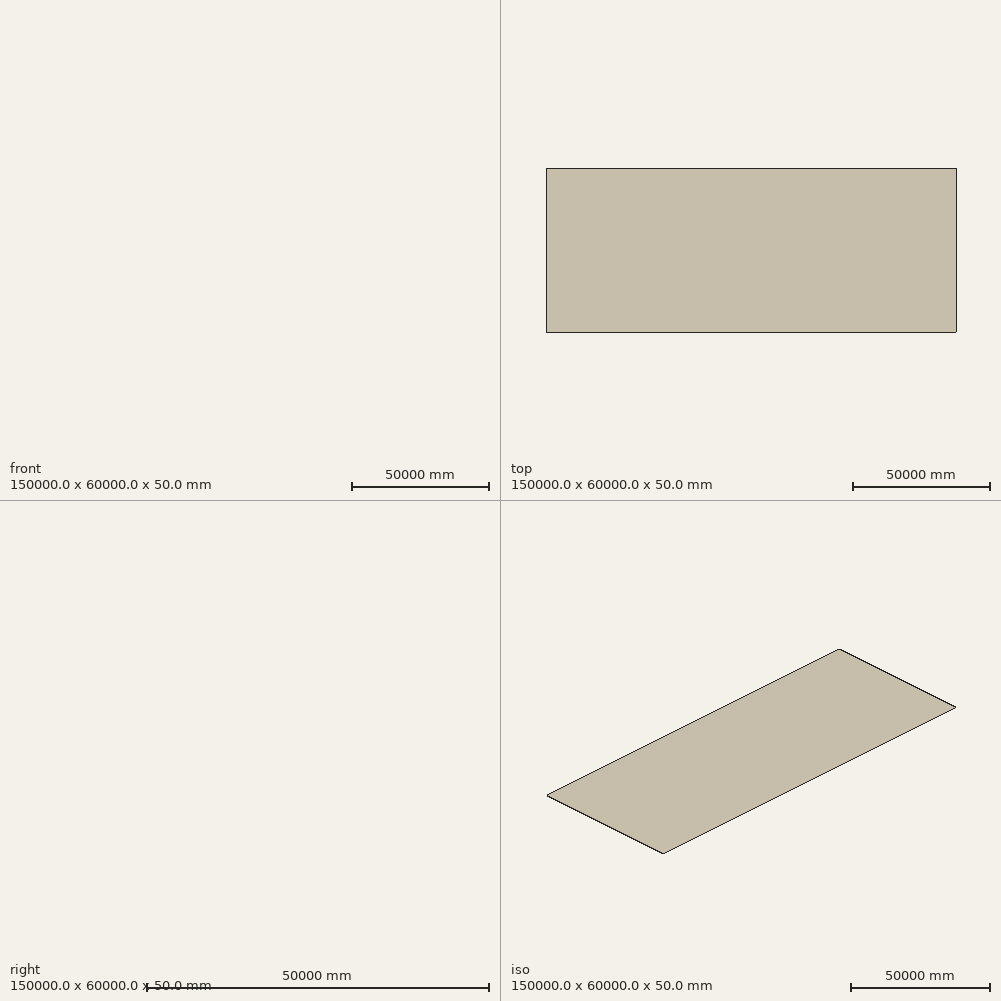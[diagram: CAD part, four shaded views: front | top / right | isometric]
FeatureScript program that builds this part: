
annotation { "Feature Type Name" : "Feature", "Feature Type Description" : "" }
export const myFeature = defineFeature(function(context is Context, id is Id, definition is map)
    precondition{}
    {
        {
            var Q0;
            Q0=qCreatedBy(makeId("Top.planeOp"),FACE);
            var sketch = newSketch(context, id + "F0", { "sketchPlane" : qUnion([Q0])});
            skLineSegment(sketch, "E0.bottom", {"start": v(-74997.93, 34015.86) * mm, "end": v(75002.07, 34015.86) * mm});
            skLineSegment(sketch, "E0.top", {"start": v(-74997.93, -25984.14) * mm, "end": v(75002.07, -25984.14) * mm});
            skLineSegment(sketch, "E0.left", {"start": v(-74997.93, 34015.86) * mm, "end": v(-74997.93, -25984.14) * mm});
            skLineSegment(sketch, "E0.right", {"start": v(75002.07, 34015.86) * mm, "end": v(75002.07, -25984.14) * mm});
            skSolve(sketch);
        }
        {
            var Q0;
            Q0=makeQuery(id+"F0.imprint","IMPRINT",FACE,{"disambiguationData":[TD([[makeQuery(id+"F0.imprint","IMPRINT",EDGE,{"derivedFrom":sQuery(id+"F0.wireOp",EDGE,"E0.bottom")}),-1.0]])]});
            extrude(context, id + "F1", {"entities" : qUnion([Q0]), "oppositeDirection" : true, "depth" : 50 * mm, "offsetDistance" : 25 * mm});
        }
    });
